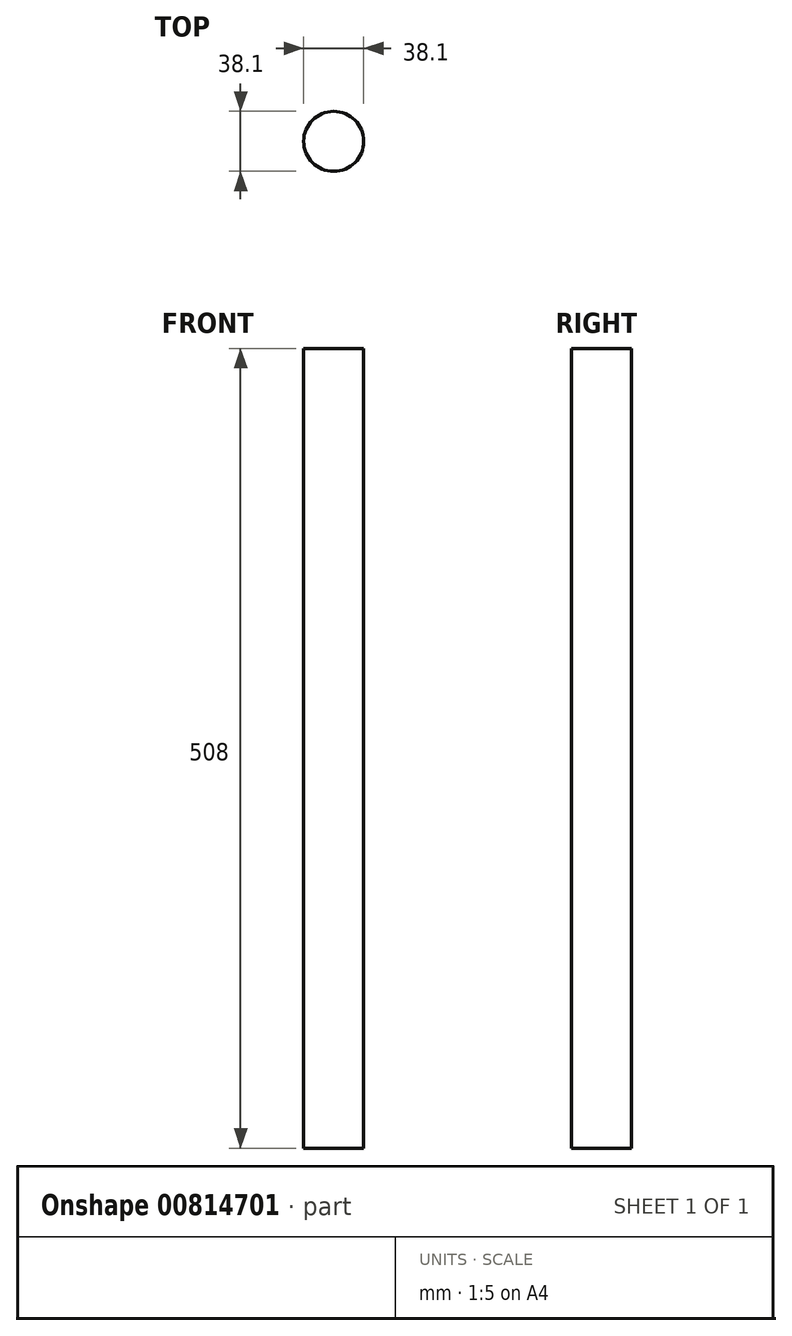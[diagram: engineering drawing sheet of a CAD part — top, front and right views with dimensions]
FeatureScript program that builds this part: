
annotation { "Feature Type Name" : "Feature", "Feature Type Description" : "" }
export const myFeature = defineFeature(function(context is Context, id is Id, definition is map)
    precondition{}
    {
        {
            var Q0;
            Q0=qCreatedBy(makeId("Top.planeOp"),FACE);
            var sketch = newSketch(context, id + "F0", { "sketchPlane" : qUnion([Q0])});
            skCircle(sketch, "E0", {"center": v(0, 0) * mm, "radius": 19.05 * mm});
            skSolve(sketch);
        }
        {
            var Q0;
            Q0=qSketchRegion(id+"F0",true);
            extrude(context, id + "F1", {"entities" : qUnion([Q0]), "depth" : 508 * mm, "offsetDistance" : 25.4 * mm});
        }
    });
